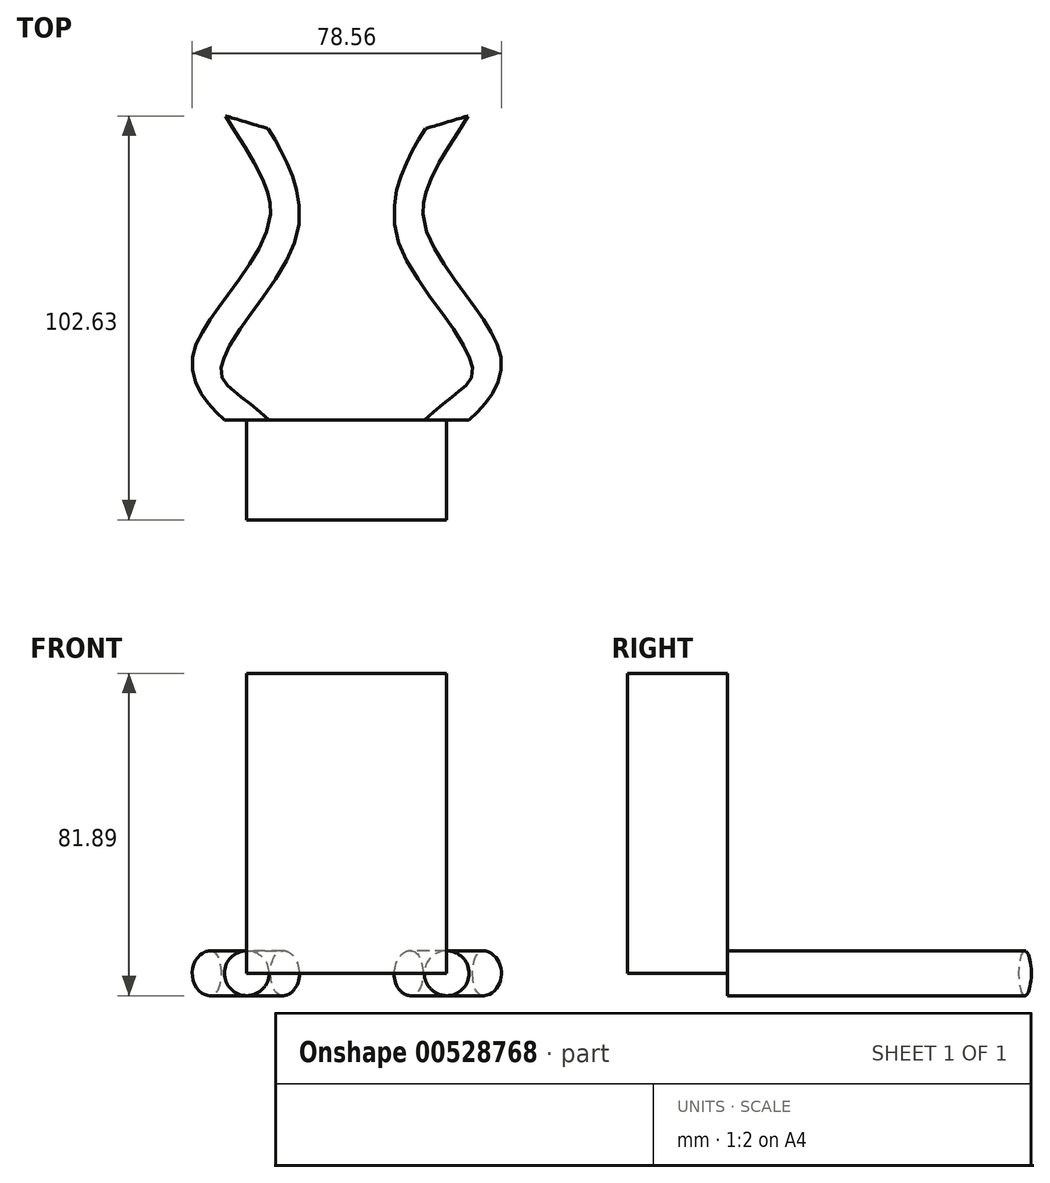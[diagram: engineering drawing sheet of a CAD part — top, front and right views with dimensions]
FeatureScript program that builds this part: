
annotation { "Feature Type Name" : "Feature", "Feature Type Description" : "" }
export const myFeature = defineFeature(function(context is Context, id is Id, definition is map)
    precondition{}
    {
        {
            var Q0;
            Q0=qCreatedBy(makeId("Front.planeOp"),FACE);
            var sketch = newSketch(context, id + "F0", { "sketchPlane" : qUnion([Q0])});
            skLineSegment(sketch, "E0.bottom", {"start": v(-50.8, 76.2) * mm, "end": v(0, 76.2) * mm});
            skLineSegment(sketch, "E0.top", {"start": v(-50.8, 0) * mm, "end": v(0, 0) * mm});
            skLineSegment(sketch, "E0.left", {"start": v(-50.8, 76.2) * mm, "end": v(-50.8, 0) * mm});
            skLineSegment(sketch, "E0.right", {"start": v(0, 76.2) * mm, "end": v(0, 0) * mm});
            skSolve(sketch);
        }
        {
            var Q0;
            Q0=makeQuery(id+"F0.imprint","IMPRINT",FACE,{"disambiguationData":[TD([[makeQuery(id+"F0.imprint","IMPRINT",EDGE,{"derivedFrom":sQuery(id+"F0.wireOp",EDGE,"E0.bottom")}),-1.0]])]});
            extrude(context, id + "F1", {"entities" : qUnion([Q0]), "depth" : 25.4 * mm, "offsetDistance" : 25.4 * mm});
        }
        {
            var Q0;
            Q0=qCreatedBy(makeId("Front.planeOp"),FACE);
            var sketch = newSketch(context, id + "F2", { "sketchPlane" : qUnion([Q0])});
            skCircle(sketch, "E1", {"center": v(0, 0) * mm, "radius": 5.69 * mm});
            skSolve(sketch);
        }
        {
            var Q0;
            Q0=qCreatedBy(makeId("Top.planeOp"),FACE);
            var sketch = newSketch(context, id + "F3", { "sketchPlane" : qUnion([Q0])});
            skFitSpline(sketch, "E2", {"points": [v(0, 0) * mm, v(9.35, 15.28) * mm, v(-8.57, 47.4) * mm, v(0, 75.62) * mm], "startDerivative": vector(57.06, 50.76) * mm, "endDerivative": vector(49.2, 79.33) * mm});
            skSolve(sketch);
        }
        {
            var Q0;
            Q0=makeQuery(id+"F2.imprint","IMPRINT",FACE,{"disambiguationData":[TD([[makeQuery(id+"F2.imprint","IMPRINT",EDGE,{"derivedFrom":sQuery(id+"F2.wireOp",EDGE,"E1")}),1.0]])]});
            var Q1;
            Q1=sQuery(id+"F3.wireOp",EDGE,"E2");
            sweep(context, id + "F4", {"profiles" : qUnion([Q0]), "path" : qUnion([Q1])});
        }
        {
            var Q0;
            Q0=qCreatedBy(makeId("Right.planeOp"),FACE);
            cPlane(context, id + "F5", {"entities" : qUnion([Q0]), "cplaneType" : CPlaneType.OFFSET, "offset" : 25.4 * mm, "oppositeDirection" : true, "width" : 152.4 * mm, "height" : 152.4 * mm});
        }
        {
            var Q0;
            Q0=makeQuery(id+"F4.opSweep","SWEPT_BODY",BODY,{"disambiguationData":[OSD([sQuery(id+"F2.wireOp",EDGE,"E1"),sQuery(id+"F3.wireOp",EDGE,"E2")])]});
            var Q1;
            Q1=qCreatedBy(id+"F5.planeOp",FACE);
            mirror(context, id + "F6", {"operationType" : NewBodyOperationType.ADD, "entities" : qUnion([Q0]), "mirrorPlane" : qUnion([Q1])});
        }
    });
